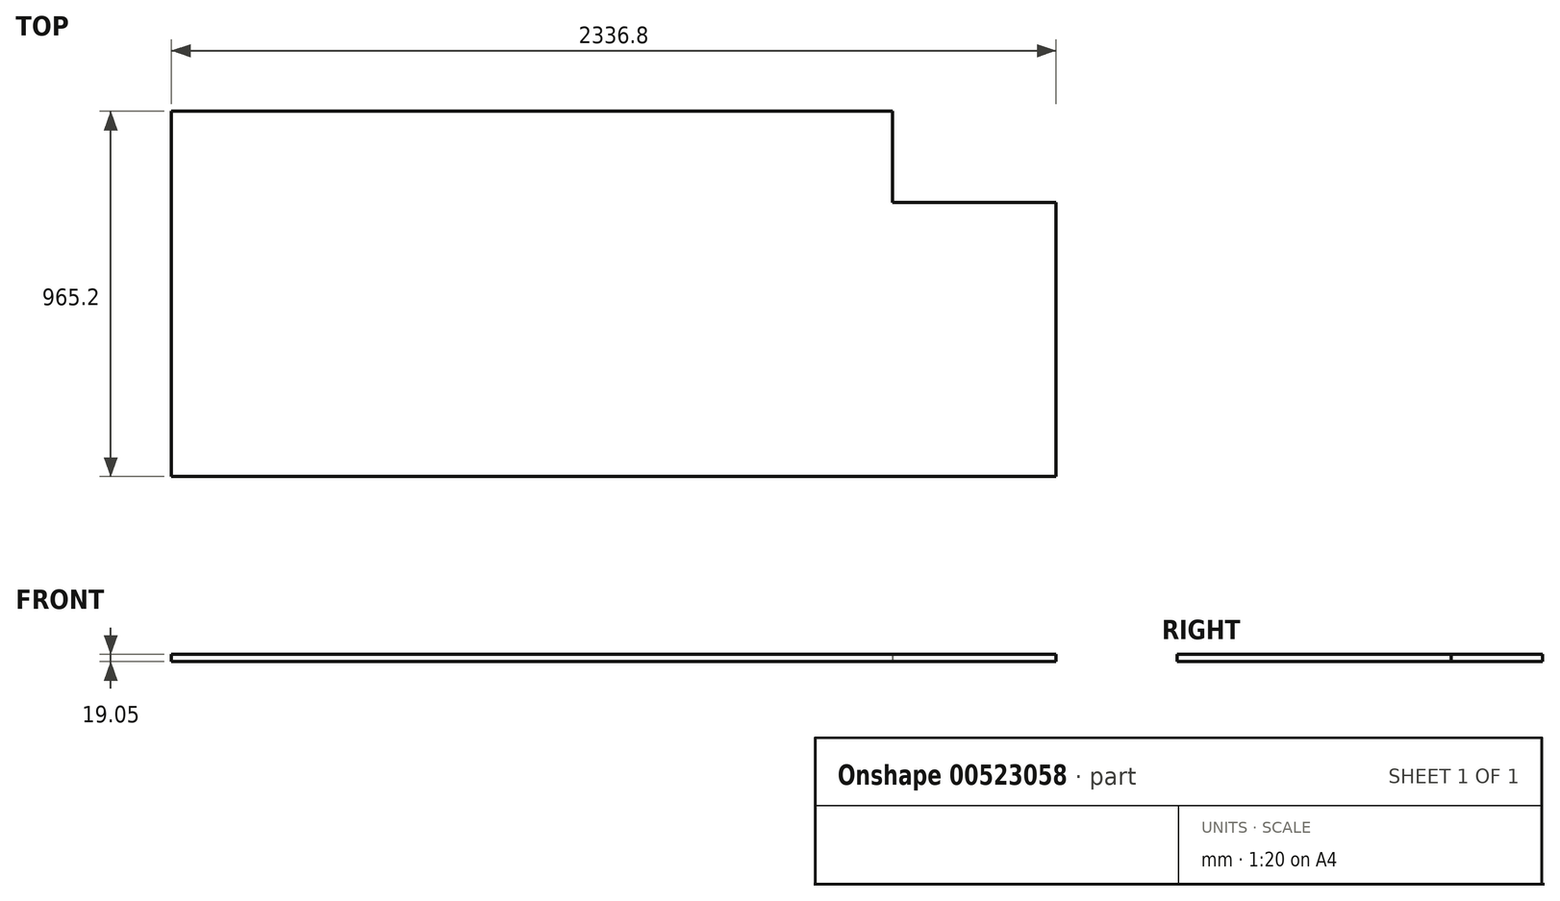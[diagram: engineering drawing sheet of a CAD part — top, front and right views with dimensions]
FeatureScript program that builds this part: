
annotation { "Feature Type Name" : "Feature", "Feature Type Description" : "" }
export const myFeature = defineFeature(function(context is Context, id is Id, definition is map)
    precondition{}
    {
        {
            var Q0;
            Q0=qCreatedBy(makeId("Top.planeOp"),FACE);
            var sketch = newSketch(context, id + "F0", { "sketchPlane" : qUnion([Q0])});
            skLineSegment(sketch, "E0.bottom", {"start": v(0, 0) * mm, "end": v(1905, 0) * mm});
            skLineSegment(sketch, "E0.top", {"start": v(0, 965.2) * mm, "end": v(1905, 965.2) * mm});
            skLineSegment(sketch, "E0.left", {"start": v(0, 0) * mm, "end": v(0, 965.2) * mm});
            skLineSegment(sketch, "E0.right", {"start": v(1905, 723.9) * mm, "end": v(1905, 965.2) * mm});
            skLineSegment(sketch, "E1.bottom", {"start": v(1905, 0) * mm, "end": v(2336.8, 0) * mm});
            skLineSegment(sketch, "E1.top", {"start": v(1905, 723.9) * mm, "end": v(2336.8, 723.9) * mm});
            skLineSegment(sketch, "E1.right", {"start": v(2336.8, 0) * mm, "end": v(2336.8, 723.9) * mm});
            skSolve(sketch);
        }
        {
            var Q0;
            Q0 = qSketchRegion(id + "F0", true);
            extrude(context, id + "F1", {"entities" : qUnion([Q0]), "depth" : 19.05 * mm, "offsetDistance" : 25.4 * mm});
        }
    });
